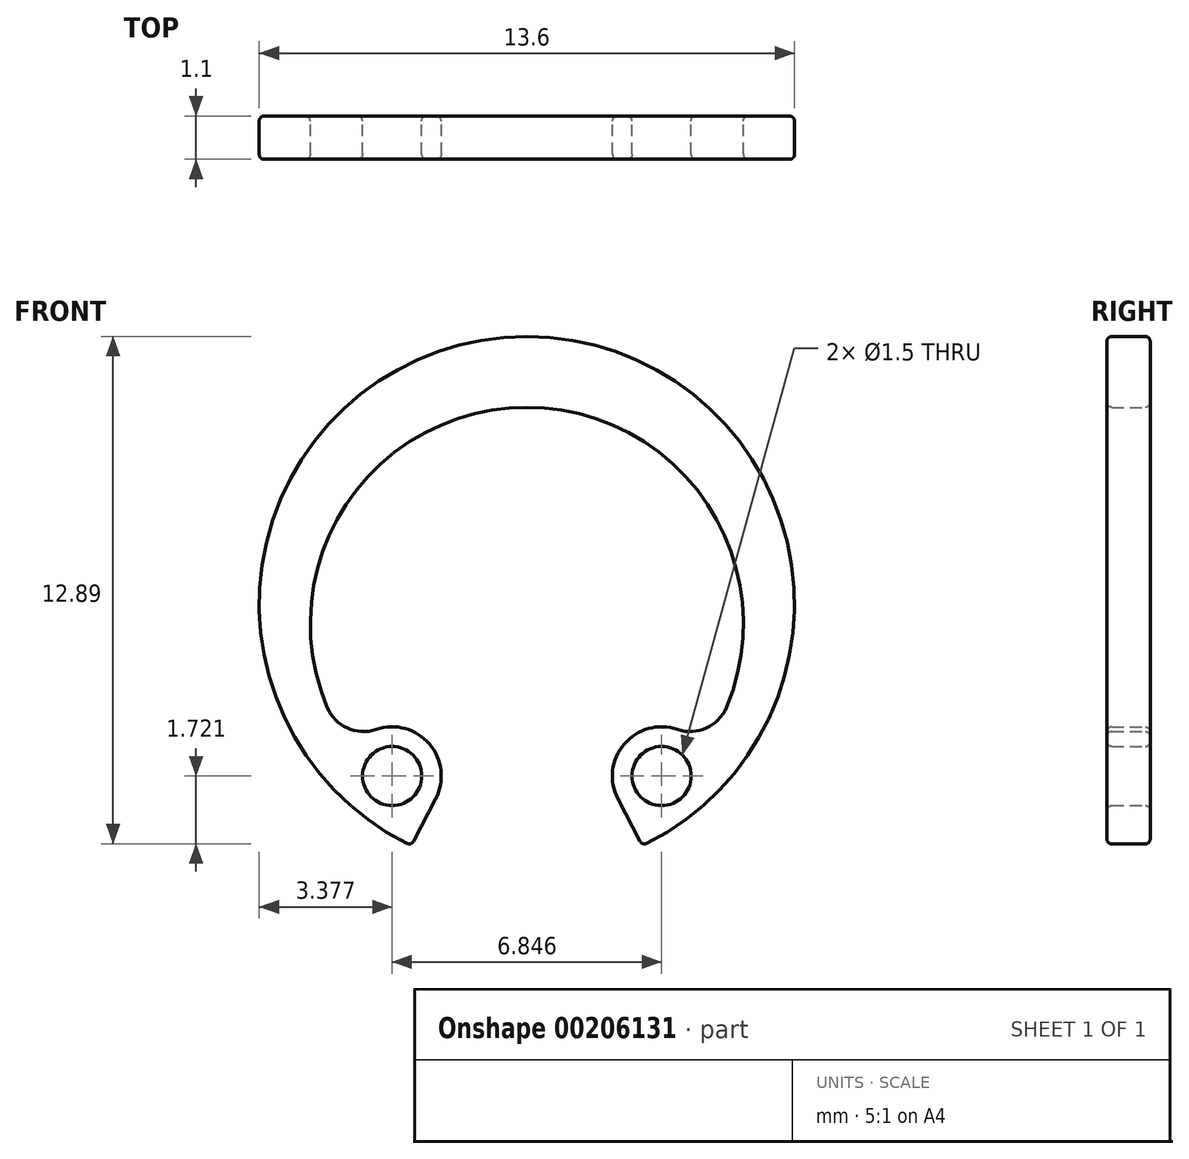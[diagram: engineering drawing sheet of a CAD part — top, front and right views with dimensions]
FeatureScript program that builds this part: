
annotation { "Feature Type Name" : "Feature", "Feature Type Description" : "" }
export const myFeature = defineFeature(function(context is Context, id is Id, definition is map)
    precondition{}
    {
        {
            var Q0;
            Q0=qCreatedBy(makeId("Front.planeOp"),FACE);
            var sketch = newSketch(context, id + "F0", { "sketchPlane" : qUnion([Q0])});
            skArc(sketch, "E0", {"start": v(2.93, -6.13) * mm, "mid": v(0, 6.8) * mm, "end": v(-2.93, -6.13) * mm});
            skPoint(sketch, "E1.first.point", {"position": v(0, 5) * mm});
            skPoint(sketch, "E1.second.point", {"position": v(0, -6) * mm});
            skPoint(sketch, "E1.third.point", {"position": v(5.48, -0.05) * mm});
            skLineSegment(sketch, "E2", {"start": v(-2.31, -4.95) * mm, "end": v(-2.93, -6.13) * mm});
            skLineSegment(sketch, "E3", {"start": v(2.31, -4.95) * mm, "end": v(2.93, -6.13) * mm});
            skLineSegment(sketch, "E4", {"start": v(-2.93, -6.13) * mm, "end": v(2.93, -6.13) * mm, "construction": true});
            skCircle(sketch, "E5", {"center": v(-3.42, -4.37) * mm, "radius": 0.75 * mm});
            skLineSegment(sketch, "E6", {"start": v(0, 1.94) * mm, "end": v(0, -8.92) * mm, "construction": true});
            skPoint(sketch, "E6.endSnap0", {"position": v(0, -6.13) * mm});
            skArc(sketch, "E7.0", {"start": v(-2.31, -4.95) * mm, "mid": v(-2.48, -3.55) * mm, "end": v(-3.83, -3.19) * mm});
            skArc(sketch, "E8.MirrorCS", {"start": v(2.31, -4.95) * mm, "mid": v(2.48, -3.55) * mm, "end": v(3.83, -3.19) * mm});
            skCircle(sketch, "E9.MirrorC", {"center": v(3.42, -4.37) * mm, "radius": 0.75 * mm});
            skArc(sketch, "E10.trimOffspring", {"start": v(5.07, -2.63) * mm, "mid": v(0, 5) * mm, "end": v(-5.07, -2.63) * mm});
            skPoint(sketch, "E11.visualSharp", {"position": v(-4.48, -3.7) * mm});
            skArc(sketch, "E11.filletArc", {"start": v(-5.07, -2.63) * mm, "mid": v(-4.56, -3.15) * mm, "end": v(-3.83, -3.19) * mm});
            skPoint(sketch, "E12.visualSharp", {"position": v(4.48, -3.7) * mm});
            skArc(sketch, "E12.filletArc", {"start": v(3.83, -3.19) * mm, "mid": v(4.56, -3.15) * mm, "end": v(5.07, -2.63) * mm});
            skSolve(sketch);
        }
        {
            var Q0;
            Q0=makeQuery(id+"F0.imprint","IMPRINT",FACE,{"disambiguationData":[TD([[makeQuery(id+"F0.imprint","IMPRINT",EDGE,{"derivedFrom":sQuery(id+"F0.wireOp",EDGE,"E0")}),1.0]])]});
            extrude(context, id + "F1", {"entities" : qUnion([Q0]), "depth" : 1.1 * mm});
        }
        {
            var Q0;
            Q0=makeQuery(id+"F1.opExtrude","CAP_FACE",FACE,{"disambiguationData":[OSD([sQuery(id+"F0.wireOp",EDGE,"E0"),sQuery(id+"F0.wireOp",EDGE,"E2"),sQuery(id+"F0.wireOp",EDGE,"E3"),sQuery(id+"F0.wireOp",EDGE,"E5"),sQuery(id+"F0.wireOp",EDGE,"E7.0"),sQuery(id+"F0.wireOp",EDGE,"E8.MirrorCS"),sQuery(id+"F0.wireOp",EDGE,"E9.MirrorC"),sQuery(id+"F0.wireOp",EDGE,"E10.trimOffspring"),sQuery(id+"F0.wireOp",EDGE,"E11.filletArc"),sQuery(id+"F0.wireOp",EDGE,"E12.filletArc")])],"isStart":false});
            var Q1;
            Q1=makeQuery(id+"F1.opExtrude","CAP_FACE",FACE,{"disambiguationData":[OSD([sQuery(id+"F0.wireOp",EDGE,"E0"),sQuery(id+"F0.wireOp",EDGE,"E2"),sQuery(id+"F0.wireOp",EDGE,"E3"),sQuery(id+"F0.wireOp",EDGE,"E5"),sQuery(id+"F0.wireOp",EDGE,"E7.0"),sQuery(id+"F0.wireOp",EDGE,"E8.MirrorCS"),sQuery(id+"F0.wireOp",EDGE,"E9.MirrorC"),sQuery(id+"F0.wireOp",EDGE,"E10.trimOffspring"),sQuery(id+"F0.wireOp",EDGE,"E11.filletArc"),sQuery(id+"F0.wireOp",EDGE,"E12.filletArc")])],"isStart":true});
            var Q2;
            Q2=makeQuery(id+"F1.opExtrude","SWEPT_EDGE",EDGE,{"disambiguationData":[OSD([sQuery(id+"F0.wireOp",EDGE,"E0"),sQuery(id+"F0.wireOp",EDGE,"E2")])]});
            var Q3;
            Q3=makeQuery(id+"F1.opExtrude","SWEPT_EDGE",EDGE,{"disambiguationData":[OSD([sQuery(id+"F0.wireOp",EDGE,"E0"),sQuery(id+"F0.wireOp",EDGE,"E3")])]});
            fillet(context, id + "F2", {"entities" : qUnion([Q0, Q1, Q2, Q3]), "radius" : 0.13 * mm, "tangentPropagation" : true, "allowEdgeOverflow" : false});
        }
    });
